# Revit family: DEVIreg 316_RFA_1
name_source: partatom
category: Data Devices
units: mm (PartAtom-declared; Revit-internal decimal feet)

## family parameters
Cut with Voids When Loaded = No
Host = Face
Maintain Annotation Orientation = No
OmniClass Number = 23.85.50.17
OmniClass Title = Communication and Data Processing Equipment
Part Type = Normal
Room Calculation Point = No
Round Connector Dimension = Use Diameter
Shared = No

## types (1)
- DEVIreg™ 316_140F1075
    Ambient Temperature Range = -10 °C to +45 °C
    Body Material = Danfoss Plastic White
    Cable specification for connector terminals, max. = 1 x 4 mm² or 2 x 2.5 mm²
    Controller type = 1 B
    D = 58 mm  [stored 0.190289 ft]
    Default Elevation = 0 mm  [stored 0 ft]
    Description = Electronic thermostat
    H = 85 mm  [stored 0.278871 ft]
    Hysteresis = 0 °C to 6 °C
    IP Rating = 30
    IfcExportAs = IfcElectricApplianceType
    IfcExportType = DEVIreg 316
    Inductive load = Max. 1 A, cos φ = 0.3
    L = 58 mm  [stored 0.190289 ft]
    LOD 200 = No
    LOD 350 = Yes
    Lowering in economy periods = 0 °C to 8 °C
    Manufacturer = Danfoss
    Marking = D316
    Minimum temperature range = -10 °C to +5 °C
    Model = 140F1075
    Model Type = DEVIreg™ 316
    Mounting method = DIN rail
    NominalHeight = 85 mm  [stored 0.278871 ft]
    NominalLength = 58 mm  [stored 0.190289 ft]
    NominalWidth = 52 mm  [stored 0.170604 ft]
    Operating Temperature Range = -10 °C to +50 °C
    Pollution degree  = 2 (domestic use)
    Power = 0 W
    Protection class = Class II
    Resistive load = Max. 16 A, 3680 W @ 230 V
    Sensing unit = NTC 15 kOhm at 25 °C
    Standby power consumption = 0.25 W
    Storage temperature = -25 °C to 60 °C, 90% RH non-condensing
    URL = https://store.danfoss.com
    Voltage = 230 V
    W = 52 mm  [stored 0.170604 ft]
    Weight = 0.18 kg

note: [stored X ft] marks values corroborated as IEEE doubles in the binary element streams (Revit-internal decimal feet)

## geometry (parser evidence)
native form markers: Sweep x2
no freeform markers — native parametric forms only
